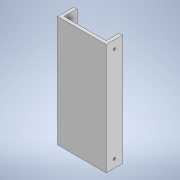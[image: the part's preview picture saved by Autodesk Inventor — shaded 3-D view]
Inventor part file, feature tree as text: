
AUTODESK INVENTOR PART (.ipt)
format: ipt  version: 2020 (Build 240168000, 168)  size: 138,752 bytes
history: native  units: mm
features: sketch x3, extrude x2, other x1, hole x1, mirror x1
ambient origin geometry x8: Origin, YZ Plane, XZ Plane, XY Plane, X Axis, Y Axis, Z Axis, Center Point
bodies: Body1 (feature_tree)
feature tree (8):
  other  "Твердое тело1"
  extrude  "Выдавливание1"  Depth=30.0mm
  sketch  "Эскиз2"
  extrude  "Выдавливание3"  Depth=10.0mm
  hole  "Отверстие1"  [1 undecoded]
  mirror  "Зеркальное отражение1"
  sketch  "Эскиз1"
  sketch  "Эскиз3"
note: 1 required parameter value undecoded (feature->parameter linkage not recoverable at this tier; creation-order binding heuristic only, values carry confidence <= 0.55)
